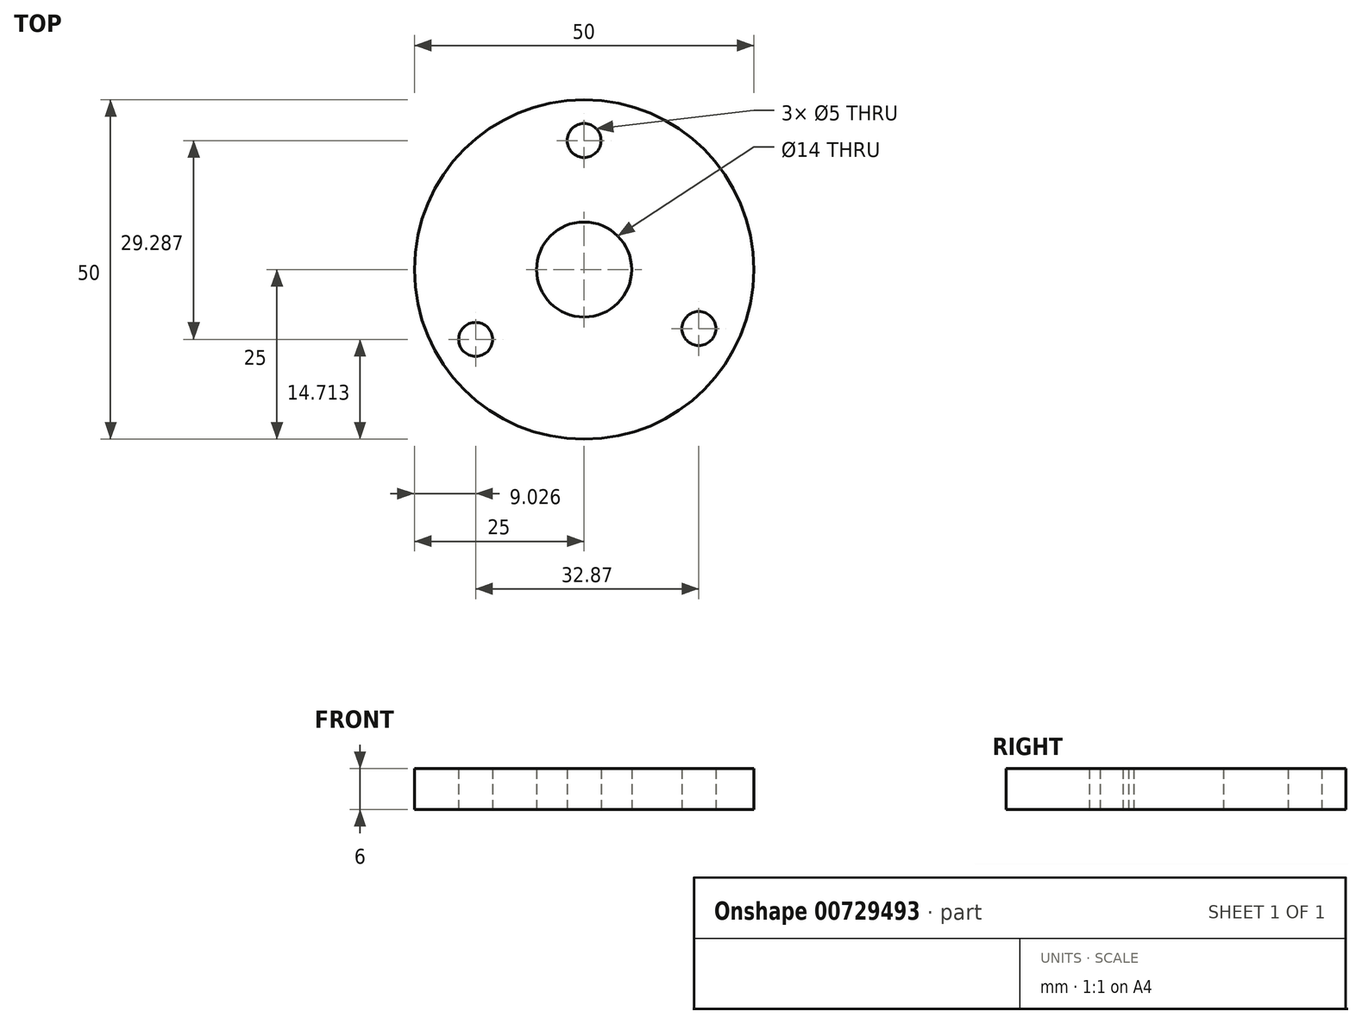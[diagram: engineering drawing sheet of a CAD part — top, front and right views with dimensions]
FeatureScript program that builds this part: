
annotation { "Feature Type Name" : "Feature", "Feature Type Description" : "" }
export const myFeature = defineFeature(function(context is Context, id is Id, definition is map)
    precondition{}
    {
        {
            var Q0;
            Q0=qCreatedBy(makeId("Top.planeOp"),FACE);
            var sketch = newSketch(context, id + "F0", { "sketchPlane" : qUnion([Q0])});
            skCircle(sketch, "E0", {"center": v(0, 0) * mm, "radius": 25 * mm});
            skCircle(sketch, "E1", {"center": v(0, 0) * mm, "radius": 7 * mm});
            skCircle(sketch, "E2", {"center": v(16.9, -8.7) * mm, "radius": 2.5 * mm});
            skCircle(sketch, "E3", {"center": v(-15.97, -10.29) * mm, "radius": 2.5 * mm});
            skLineSegment(sketch, "E4", {"start": v(0, 0) * mm, "end": v(16.9, -8.7) * mm, "construction": true});
            skLineSegment(sketch, "E5", {"start": v(0, 0) * mm, "end": v(-15.97, -10.29) * mm, "construction": true});
            skLineSegment(sketch, "E6", {"start": v(0, 0) * mm, "end": v(0, 19) * mm});
            skCircle(sketch, "E7", {"center": v(0, 19) * mm, "radius": 2.5 * mm});
            skSolve(sketch);
        }
        {
            var Q0;
            Q0=makeQuery(id+"F0.imprint","IMPRINT",FACE,{"disambiguationData":[TD([[makeQuery(id+"F0.imprint","IMPRINT",EDGE,{"derivedFrom":sQuery(id+"F0.wireOp",EDGE,"E0")}),1.0]])]});
            extrude(context, id + "F1", {"entities" : qUnion([Q0]), "depth" : 6 * mm, "offsetDistance" : 25 * mm});
        }
    });
